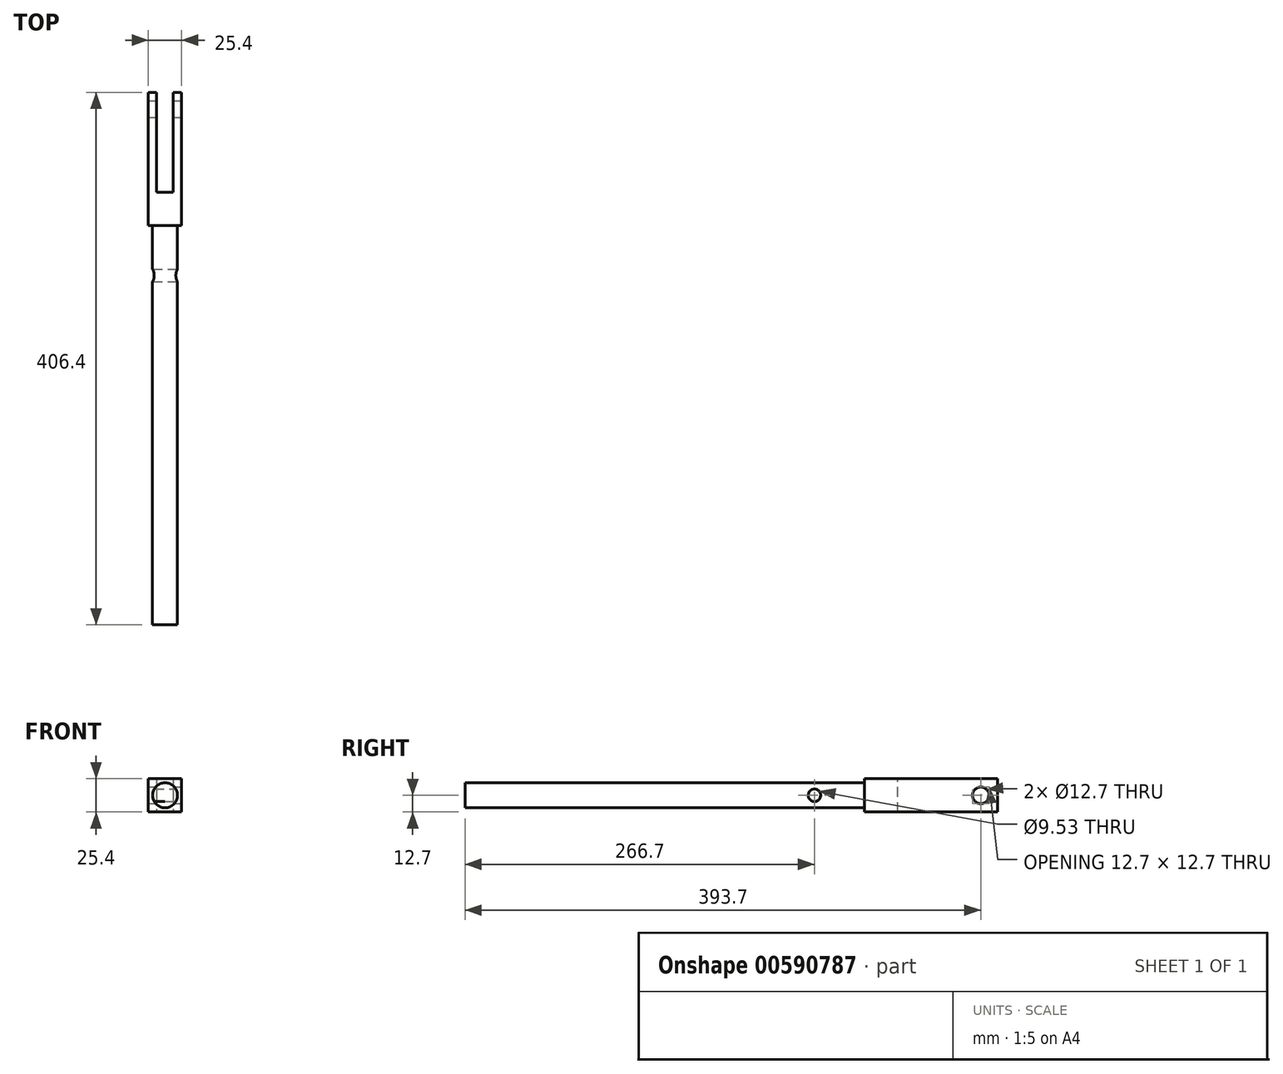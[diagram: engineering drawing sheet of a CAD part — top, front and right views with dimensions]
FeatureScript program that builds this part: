
annotation { "Feature Type Name" : "Feature", "Feature Type Description" : "" }
export const myFeature = defineFeature(function(context is Context, id is Id, definition is map)
    precondition{}
    {
        {
            var Q0;
            Q0=qCreatedBy(makeId("Top.planeOp"),FACE);
            var sketch = newSketch(context, id + "F0", { "sketchPlane" : qUnion([Q0])});
            skLineSegment(sketch, "E0.bottom", {"start": v(12.7, 50.8) * mm, "end": v(-12.7, 50.8) * mm});
            skLineSegment(sketch, "E0.top", {"start": v(12.7, -50.8) * mm, "end": v(-12.7, -50.8) * mm});
            skLineSegment(sketch, "E0.left", {"start": v(12.7, 50.8) * mm, "end": v(12.7, -50.8) * mm});
            skLineSegment(sketch, "E0.right", {"start": v(-12.7, 50.8) * mm, "end": v(-12.7, -50.8) * mm});
            skPoint(sketch, "E0.middle", {"position": v(0, 0) * mm});
            skSolve(sketch);
        }
        {
            var Q0;
            Q0 = qSketchRegion(id + "F0", true);
            extrude(context, id + "F1", {"entities" : qUnion([Q0]), "depth" : 25.4 * mm, "offsetDistance" : 25.4 * mm});
        }
        {
            var Q0;
            Q0=makeQuery(id+"F1.opExtrude","CAP_FACE",FACE,{"disambiguationData":[OSD([sQuery(id+"F0.wireOp",EDGE,"E0.bottom"),sQuery(id+"F0.wireOp",EDGE,"E0.top"),sQuery(id+"F0.wireOp",EDGE,"E0.left"),sQuery(id+"F0.wireOp",EDGE,"E0.right")])],"isStart":false});
            var sketch = newSketch(context, id + "F2", { "sketchPlane" : qUnion([Q0])});
            skLineSegment(sketch, "E1.bottom", {"start": v(6.35, 76.2) * mm, "end": v(-6.35, 76.2) * mm});
            skLineSegment(sketch, "E1.top", {"start": v(6.35, -25.4) * mm, "end": v(-6.35, -25.4) * mm});
            skLineSegment(sketch, "E1.left", {"start": v(6.35, 76.2) * mm, "end": v(6.35, -25.4) * mm});
            skLineSegment(sketch, "E1.right", {"start": v(-6.35, 76.2) * mm, "end": v(-6.35, -25.4) * mm});
            skPoint(sketch, "E1.middle", {"position": v(0, 25.4) * mm});
            skSolve(sketch);
        }
        {
            var Q0;
            Q0 = qSketchRegion(id + "F2", true);
            extrude(context, id + "F3", {"entities" : qUnion([Q0]), "operationType" : NewBodyOperationType.REMOVE, "endBound" : BoundingType.THROUGH_ALL, "oppositeDirection" : true, "depth" : 25.4 * mm, "offsetDistance" : 25.4 * mm});
        }
        {
            var Q0;
            Q0=makeQuery(id+"F1.opExtrude","SWEPT_FACE",FACE,{"disambiguationData":[OSD([sQuery(id+"F0.wireOp",EDGE,"E0.left")])]});
            var sketch = newSketch(context, id + "F4", { "sketchPlane" : qUnion([Q0])});
            skCircle(sketch, "E2", {"center": v(38.1, 12.7) * mm, "radius": 6.35 * mm});
            skPoint(sketch, "E2.centerSnap0", {"position": v(50.8, 12.7) * mm});
            skSolve(sketch);
        }
        {
            var Q0;
            Q0 = qSketchRegion(id + "F4", true);
            extrude(context, id + "F5", {"entities" : qUnion([Q0]), "operationType" : NewBodyOperationType.REMOVE, "endBound" : BoundingType.THROUGH_ALL, "oppositeDirection" : true, "depth" : 25.4 * mm, "offsetDistance" : 25.4 * mm});
        }
        {
            var Q0;
            Q0=makeQuery(id+"F1.opExtrude","SWEPT_FACE",FACE,{"disambiguationData":[OSD([sQuery(id+"F0.wireOp",EDGE,"E0.top")])]});
            var sketch = newSketch(context, id + "F6", { "sketchPlane" : qUnion([Q0])});
            skCircle(sketch, "E3", {"center": v(0, 12.7) * mm, "radius": 9.53 * mm});
            skPoint(sketch, "E3.centerSnap0", {"position": v(12.7, 12.7) * mm});
            skSolve(sketch);
        }
        {
            var Q0;
            Q0 = qSketchRegion(id + "F6", true);
            extrude(context, id + "F7", {"entities" : qUnion([Q0]), "operationType" : NewBodyOperationType.ADD, "depth" : 304.8 * mm, "offsetDistance" : 25.4 * mm});
        }
        {
            var Q0;
            Q0=makeQuery(id+"F1.opExtrude","SWEPT_FACE",FACE,{"disambiguationData":[OSD([sQuery(id+"F0.wireOp",EDGE,"E0.left")])]});
            var sketch = newSketch(context, id + "F8", { "sketchPlane" : qUnion([Q0])});
            skCircle(sketch, "E4", {"center": v(-88.9, 12.7) * mm, "radius": 4.76 * mm});
            skPoint(sketch, "E4.centerSnap0", {"position": v(-50.8, 12.7) * mm});
            skSolve(sketch);
        }
        {
            var Q0;
            Q0 = qSketchRegion(id + "F8", true);
            extrude(context, id + "F9", {"entities" : qUnion([Q0]), "operationType" : NewBodyOperationType.REMOVE, "endBound" : BoundingType.THROUGH_ALL, "oppositeDirection" : true, "depth" : 25.4 * mm, "offsetDistance" : 25.4 * mm});
        }
    });
